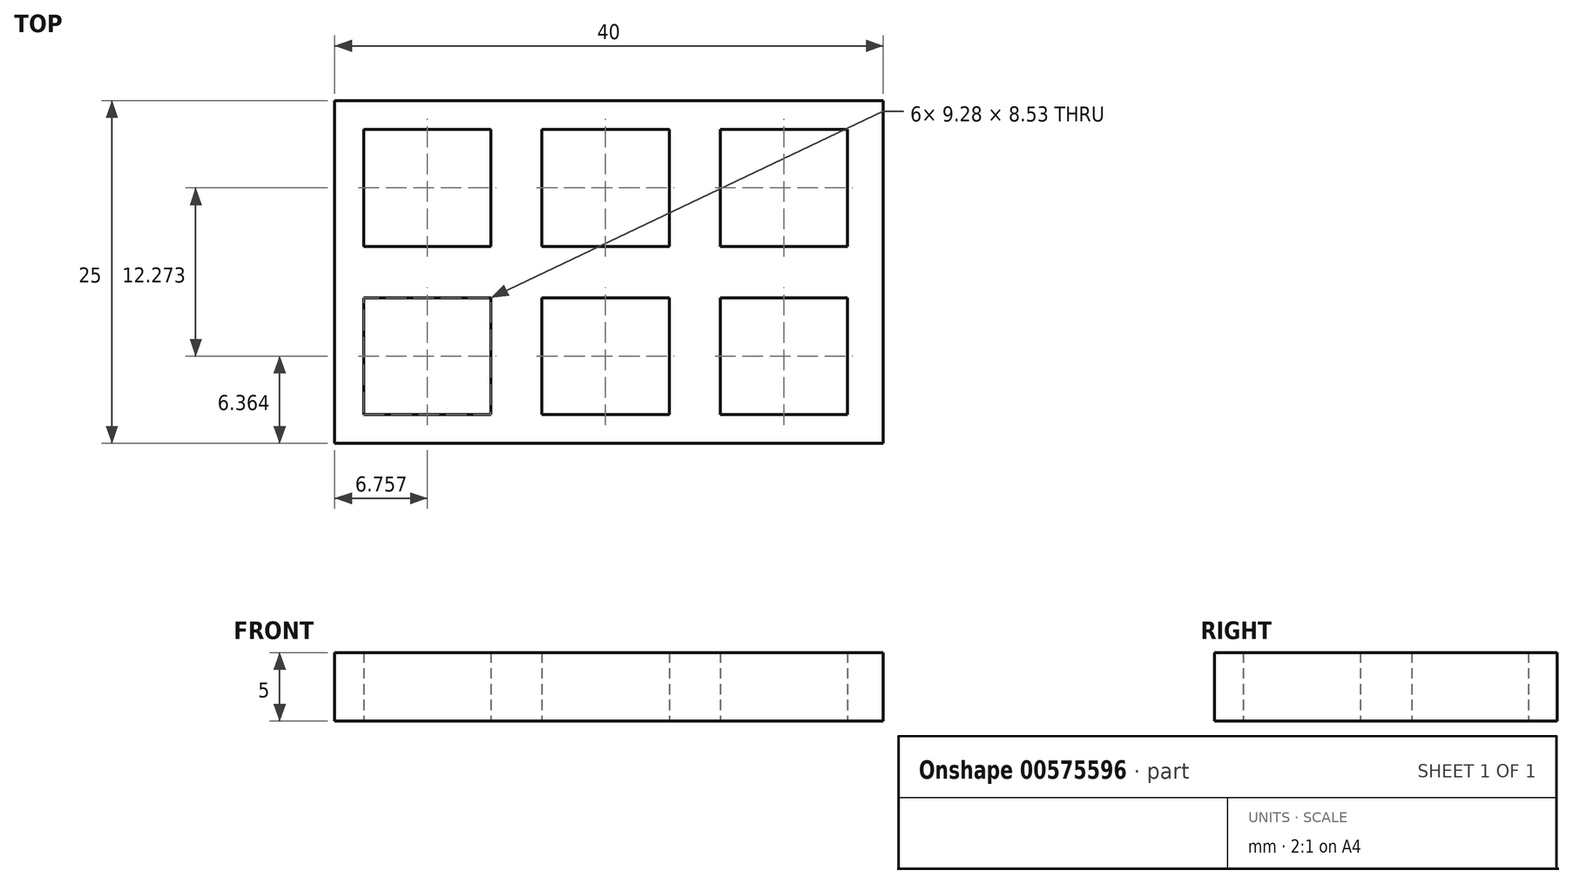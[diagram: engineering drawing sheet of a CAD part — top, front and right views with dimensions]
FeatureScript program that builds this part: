
annotation { "Feature Type Name" : "Feature", "Feature Type Description" : "" }
export const myFeature = defineFeature(function(context is Context, id is Id, definition is map)
    precondition{}
    {
        {
            var Q0;
            Q0=qCreatedBy(makeId("Top.planeOp"),FACE);
            var sketch = newSketch(context, id + "F0", { "sketchPlane" : qUnion([Q0])});
            skLineSegment(sketch, "E0.bottom", {"start": v(0, 0) * mm, "end": v(40, 0) * mm});
            skLineSegment(sketch, "E0.top", {"start": v(0, 25) * mm, "end": v(40, 25) * mm});
            skLineSegment(sketch, "E0.left", {"start": v(0, 0) * mm, "end": v(0, 25) * mm});
            skLineSegment(sketch, "E0.right", {"start": v(40, 0) * mm, "end": v(40, 25) * mm});
            skLineSegment(sketch, "E1", {"start": v(0, 12.5) * mm, "end": v(48.78, 12.5) * mm, "construction": true});
            skLineSegment(sketch, "E2.bottom", {"start": v(2.12, 2.1) * mm, "end": v(11.4, 2.1) * mm});
            skLineSegment(sketch, "E2.top", {"start": v(2.12, 10.63) * mm, "end": v(11.4, 10.63) * mm});
            skLineSegment(sketch, "E2.left", {"start": v(2.12, 2.1) * mm, "end": v(2.12, 10.63) * mm});
            skLineSegment(sketch, "E2.right", {"start": v(11.4, 2.1) * mm, "end": v(11.4, 10.63) * mm});
            skLineSegment(sketch, "E3.1.0.0", {"start": v(24.4, 2.1) * mm, "end": v(24.4, 10.63) * mm});
            skLineSegment(sketch, "E3.1.0.1", {"start": v(15.12, 10.63) * mm, "end": v(24.4, 10.63) * mm});
            skLineSegment(sketch, "E3.1.0.2", {"start": v(15.12, 2.1) * mm, "end": v(15.12, 10.63) * mm});
            skLineSegment(sketch, "E3.1.0.3", {"start": v(15.12, 2.1) * mm, "end": v(24.4, 2.1) * mm});
            skLineSegment(sketch, "E3.2.0.0", {"start": v(37.4, 2.1) * mm, "end": v(37.4, 10.63) * mm});
            skLineSegment(sketch, "E3.2.0.1", {"start": v(28.12, 10.63) * mm, "end": v(37.4, 10.63) * mm});
            skLineSegment(sketch, "E3.2.0.2", {"start": v(28.12, 2.1) * mm, "end": v(28.12, 10.63) * mm});
            skLineSegment(sketch, "E3.2.0.3", {"start": v(28.12, 2.1) * mm, "end": v(37.4, 2.1) * mm});
            skLineSegment(sketch, "E3.direction1", {"start": v(2.12, 2.1) * mm, "end": v(15.12, 2.1) * mm, "construction": true});
            skLineSegment(sketch, "E4.MirrorCS", {"start": v(2.12, 14.37) * mm, "end": v(11.4, 14.37) * mm});
            skLineSegment(sketch, "E5.MirrorCS", {"start": v(11.4, 22.9) * mm, "end": v(11.4, 14.37) * mm});
            skLineSegment(sketch, "E6.MirrorCS", {"start": v(2.12, 22.9) * mm, "end": v(2.12, 14.37) * mm});
            skLineSegment(sketch, "E7.MirrorCS", {"start": v(15.12, 22.9) * mm, "end": v(15.12, 14.37) * mm});
            skLineSegment(sketch, "E8.MirrorCS", {"start": v(15.12, 14.37) * mm, "end": v(24.4, 14.37) * mm});
            skLineSegment(sketch, "E9.MirrorCS", {"start": v(24.4, 22.9) * mm, "end": v(24.4, 14.37) * mm});
            skLineSegment(sketch, "E10.MirrorCS", {"start": v(15.12, 22.9) * mm, "end": v(24.4, 22.9) * mm});
            skLineSegment(sketch, "E11.MirrorCS", {"start": v(28.12, 22.9) * mm, "end": v(28.12, 14.37) * mm});
            skLineSegment(sketch, "E12.MirrorCS", {"start": v(28.12, 14.37) * mm, "end": v(37.4, 14.37) * mm});
            skLineSegment(sketch, "E13.MirrorCS", {"start": v(37.4, 22.9) * mm, "end": v(37.4, 14.37) * mm});
            skLineSegment(sketch, "E14.MirrorCS", {"start": v(28.12, 22.9) * mm, "end": v(37.4, 22.9) * mm});
            skLineSegment(sketch, "E15", {"start": v(2.12, 22.9) * mm, "end": v(11.4, 22.9) * mm});
            skSolve(sketch);
        }
        {
            var Q0;
            Q0=makeQuery(id+"F0.imprint","IMPRINT",FACE,{"disambiguationData":[TD([[makeQuery(id+"F0.imprint","IMPRINT",EDGE,{"derivedFrom":sQuery(id+"F0.wireOp",EDGE,"E0.bottom")}),1.0]])]});
            extrude(context, id + "F1", {"entities" : qUnion([Q0]), "depth" : 5 * mm, "offsetDistance" : 25 * mm});
        }
    });
